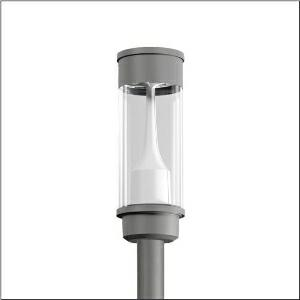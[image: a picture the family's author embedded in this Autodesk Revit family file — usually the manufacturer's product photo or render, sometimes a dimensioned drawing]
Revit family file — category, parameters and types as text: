
# Revit family: litepole_iq___st1_2a_5xa5415af14h_245c
name_source: partatom
category: Lighting Fixtures
units: mm (PartAtom-declared; Revit-internal decimal feet)

## family parameters
Cut with Voids When Loaded = No
Host = Face
Light Source = No
Part Type = Normal
Room Calculation Point = No
Round Connector Dimension = Use Diameter
Shared = No

## types (1)
- --- (1 x LED, 1540 lm, 12.9 W, 2200K)
    Apparent Load = 13 VA
    CIE Flux Codes = 22 61 93 96 100
    Color Rendering = 70
    Color Temperature = 2200K
    Default Elevation = 1800 mm
    Description = Litepole iQ, mast luminaire, Module 540 iQ-SR, primary light control with 3 zone facetted reflector, of plastic, silver coated, highly specular, structured, primary optical cover: cover, of PMMA, transparent, partly coated, light distribution: ST1.2a, light emission: direct distribution, primary light characteristic: asymmetric, installation type: post-top, LED, High Power LED, rated luminous flux: 1.540lm, luminous efficacy: 119lm/W, light colour: 722, colour temperature: 2200K, control gear: ECG iQ, control: optimised constant luminous flux control (CLO 2.0), Desk-Remote (wireless, voltage-free reading and setting of iQ features in the workshop via application-optimized NFC function/RFID function), Light-Fading, Smart-Wire, Night-Set, Lumen-Switch, Temp-Guard, Auto-Match, Street-Remote, presetting dimming logarithmic, with terminal, 6-pole, max. 2.5mm², mains connection: 220..240V, AC, 50/60Hz, start of lifetime: 13W, end of lifetime: 13W, reduction: 6W, luminaire housing, upper part, of glass-fibre reinforced polyester, coated, Siteco® metallic grey (DB 702S), diameter: 210mm, height: 590mm, spigot size: d x l = 76 x 70mm (post-top) | with reducer (optional accessory) 60 x 70mm, post-top mast mounting element, of diecast aluminium, coated, Siteco® metallic grey (DB 702S), Module 540 iQ-SR, traffic white (RAL 9016), equipment: standard, protection rating (complete): IP65, insulation class (complete): insulation class II (safety insulation), certification: CE, ENEC, VDE, packaging unit: 1 piece

Light Distribution: ST1.2a
    Height = 590 mm
    Lamp = 1 x LED
    Lamp Light Flux = 1540 lm
    Lamp Power = 12.9 W
    Lamp count = 1
    Length = 220 mm
    Luminous efficacy = 119 lm/W
    Manufacturer = Siteco
    ModVariant = No
    Model = 5XA5415AF14H
    Number of Poles = 1
    OnlyDefault = Yes
    Power Factor = 1
    Product Name = Litepole iQ | ST1.2a
    Product group = mast luminaire | pylon top
    ProductGroupID = 6100
    Protection Class = Protection class II
    Protection Degree = IP 65
    RLX_Detail_Level = 1
    RlxData = <blob elided: 72353 chars, md5=97beb129>
    Socket = socket
    Standby Power = 0 W
    System Light Flux = 1540 lm
    System Power = 13 W
    Type Comments = factory setting: luminous flux: 100 % | dim-lin: 254 | 516 mA
    Type Image = l_1006025.jpg
    URL = http://relux.com
    VarID = @adj_070137
    Voltage = 0 V
    Weight = 0.00 kg
    Width = 0 mm  [stored 0 ft]

note: [stored X ft] marks values corroborated as IEEE doubles in the binary element streams (Revit-internal decimal feet)

## geometry (parser evidence)
native form markers: Blend x4, Sweep x10
no freeform markers — native parametric forms only
